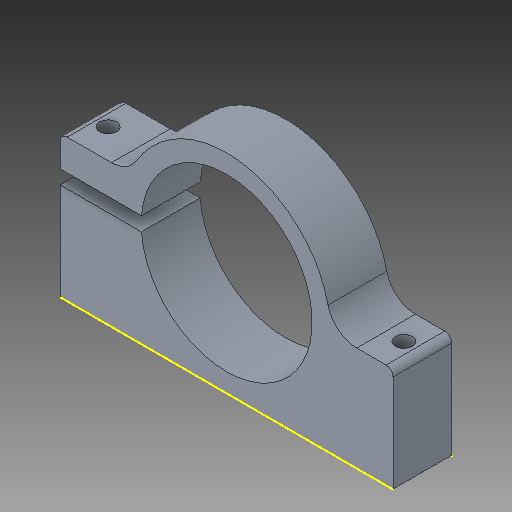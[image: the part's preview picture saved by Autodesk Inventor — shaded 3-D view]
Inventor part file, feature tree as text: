
AUTODESK INVENTOR PART (.ipt)
format: ipt  version: 2017 (Build 210142000, 142)  size: 151,040 bytes
history: native  units: in
note: dims shown in document units (in); Inventor stores cm internally (conversion verified against a paired STEP export)
features: other x7, sketch x1
ambient origin geometry x8: Origin, YZ Plane, XZ Plane, XY Plane, X Axis, Y Axis, Z Axis, Center Point
bodies: Solid1 (feature_tree)
feature tree (8):
  other  "tetrix_739089_2012"
  other  "A_2"
  other  "A_3"
  other  "A_4"
  other  "FRONT"
  other  "TOP"
  other  "RIGHT"
  sketch  "Sketch1"
